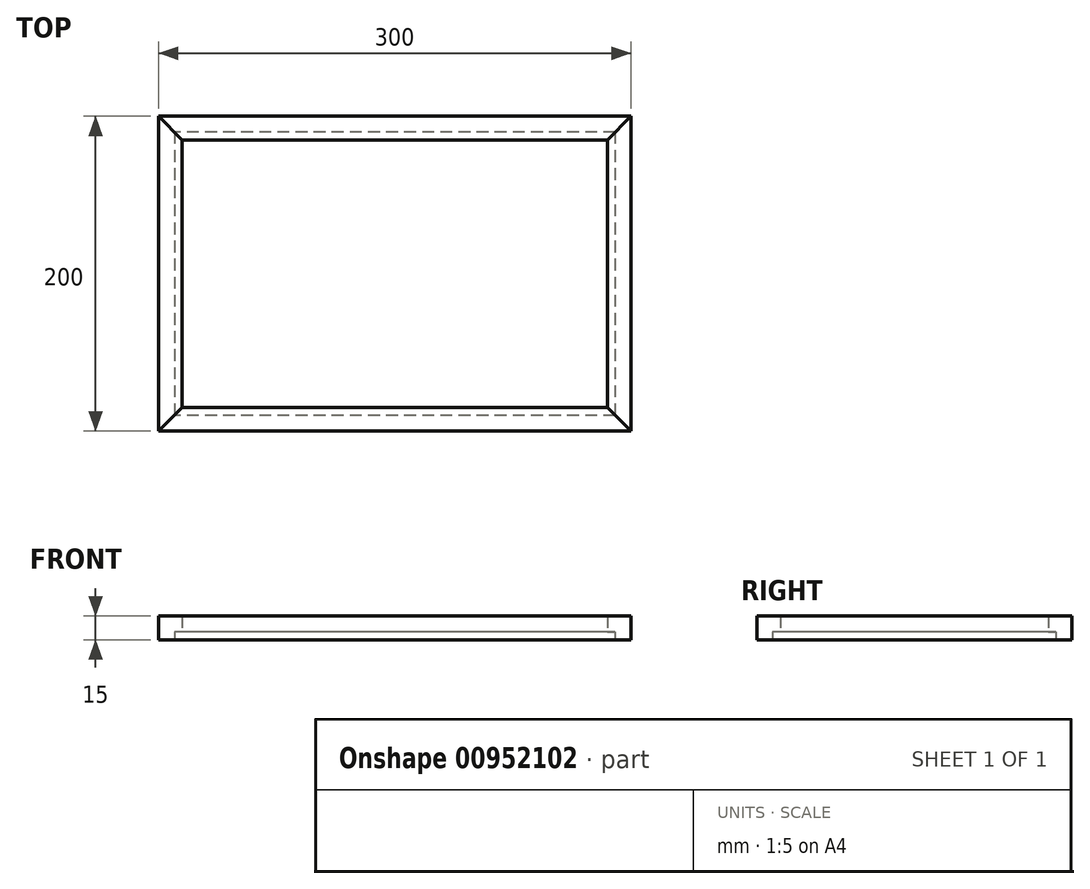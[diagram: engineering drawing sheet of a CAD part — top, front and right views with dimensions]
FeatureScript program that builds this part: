
annotation { "Feature Type Name" : "Feature", "Feature Type Description" : "" }
export const myFeature = defineFeature(function(context is Context, id is Id, definition is map)
    precondition{}
    {
        {
            var Q0;
            Q0=qCreatedBy(makeId("Top.planeOp"),FACE);
            var sketch = newSketch(context, id + "F0", { "sketchPlane" : qUnion([Q0])});
            skLineSegment(sketch, "E0.bottom", {"start": v(150, 100) * mm, "end": v(-150, 100) * mm});
            skLineSegment(sketch, "E0.top", {"start": v(150, -100) * mm, "end": v(-150, -100) * mm});
            skLineSegment(sketch, "E0.left", {"start": v(150, 100) * mm, "end": v(150, -100) * mm});
            skLineSegment(sketch, "E0.right", {"start": v(-150, 100) * mm, "end": v(-150, -100) * mm});
            skPoint(sketch, "E0.middle", {"position": v(0, 0) * mm});
            skLineSegment(sketch, "E1.0", {"start": v(135, 85) * mm, "end": v(-135, 85) * mm});
            skLineSegment(sketch, "E1.1", {"start": v(135, 85) * mm, "end": v(135, -85) * mm});
            skLineSegment(sketch, "E1.2", {"start": v(135, -85) * mm, "end": v(-135, -85) * mm});
            skLineSegment(sketch, "E1.3", {"start": v(-135, 85) * mm, "end": v(-135, -85) * mm});
            skLineSegment(sketch, "E2", {"start": v(-135, 85) * mm, "end": v(-150, 100) * mm});
            skLineSegment(sketch, "E3", {"start": v(135, 85) * mm, "end": v(150, 100) * mm});
            skLineSegment(sketch, "E4", {"start": v(135, -85) * mm, "end": v(150, -100) * mm});
            skLineSegment(sketch, "E5", {"start": v(-135, -85) * mm, "end": v(-150, -100) * mm});
            skLineSegment(sketch, "E6.0", {"start": v(140, 90) * mm, "end": v(-140, 90) * mm});
            skLineSegment(sketch, "E7.0", {"start": v(-140, 90) * mm, "end": v(-140, -90) * mm});
            skLineSegment(sketch, "E8.0", {"start": v(140, -90) * mm, "end": v(-140, -90) * mm});
            skLineSegment(sketch, "E9.0", {"start": v(140, 90) * mm, "end": v(140, -90) * mm});
            skSolve(sketch);
        }
        {
            var Q0;
            Q0=makeQuery(id+"F0.imprint","IMPRINT",FACE,{"disambiguationData":[TD([[makeQuery(id+"F0.imprint","IMPRINT",EDGE,{"derivedFrom":sQuery(id+"F0.wireOp",EDGE,"E0.bottom")}),1.0]])]});
            var Q1;
            Q1=makeQuery(id+"F0.imprint","IMPRINT",FACE,{"disambiguationData":[TD([[makeQuery(id+"F0.imprint","IMPRINT",EDGE,{"derivedFrom":sQuery(id+"F0.wireOp",EDGE,"E0.top")}),-1.0]])]});
            var Q2;
            {var subQ0=sQuery(id+"F0.wireOp",EDGE,"E1.0");Q2=makeQuery(id+"F0.imprint","IMPRINT",FACE,{"disambiguationData":[TD([[makeQuery(id+"F0.imprint","IMPRINT",EDGE,{"derivedFrom":subQ0}),-1.0]])]});}
            var Q3;
            {var subQ0=sQuery(id+"F0.wireOp",EDGE,"E1.2");Q3=makeQuery(id+"F0.imprint","IMPRINT",FACE,{"disambiguationData":[TD([[makeQuery(id+"F0.imprint","IMPRINT",EDGE,{"derivedFrom":subQ0}),1.0]])]});}
            extrude(context, id + "F1", {"entities" : qUnion([Q0, Q1, Q2, Q3]), "depth" : 15 * mm, "offsetDistance" : 25 * mm});
        }
        {
            var Q0;
            Q0=makeQuery(id+"F0.imprint","IMPRINT",FACE,{"disambiguationData":[TD([[makeQuery(id+"F0.imprint","IMPRINT",EDGE,{"derivedFrom":sQuery(id+"F0.wireOp",EDGE,"E0.right")}),1.0]])]});
            var Q1;
            Q1=makeQuery(id+"F0.imprint","IMPRINT",FACE,{"disambiguationData":[TD([[makeQuery(id+"F0.imprint","IMPRINT",EDGE,{"derivedFrom":sQuery(id+"F0.wireOp",EDGE,"E0.left")}),-1.0]])]});
            var Q2;
            {var subQ0=sQuery(id+"F0.wireOp",EDGE,"E1.3");Q2=makeQuery(id+"F0.imprint","IMPRINT",FACE,{"disambiguationData":[TD([[makeQuery(id+"F0.imprint","IMPRINT",EDGE,{"derivedFrom":subQ0}),-1.0]])]});}
            var Q3;
            {var subQ0=sQuery(id+"F0.wireOp",EDGE,"E1.1");Q3=makeQuery(id+"F0.imprint","IMPRINT",FACE,{"disambiguationData":[TD([[makeQuery(id+"F0.imprint","IMPRINT",EDGE,{"derivedFrom":subQ0}),1.0]])]});}
            extrude(context, id + "F2", {"entities" : qUnion([Q0, Q1, Q2, Q3]), "depth" : 15 * mm, "offsetDistance" : 25 * mm});
        }
        {
            var Q0;
            {var subQ0=sQuery(id+"F0.wireOp",EDGE,"E1.2");Q0=makeQuery(id+"F0.imprint","IMPRINT",FACE,{"disambiguationData":[TD([[makeQuery(id+"F0.imprint","IMPRINT",EDGE,{"derivedFrom":subQ0}),1.0]])]});}
            var Q1;
            {var subQ0=sQuery(id+"F0.wireOp",EDGE,"E1.1");Q1=makeQuery(id+"F0.imprint","IMPRINT",FACE,{"disambiguationData":[TD([[makeQuery(id+"F0.imprint","IMPRINT",EDGE,{"derivedFrom":subQ0}),1.0]])]});}
            var Q2;
            {var subQ0=sQuery(id+"F0.wireOp",EDGE,"E1.0");Q2=makeQuery(id+"F0.imprint","IMPRINT",FACE,{"disambiguationData":[TD([[makeQuery(id+"F0.imprint","IMPRINT",EDGE,{"derivedFrom":subQ0}),-1.0]])]});}
            var Q3;
            {var subQ0=sQuery(id+"F0.wireOp",EDGE,"E1.3");Q3=makeQuery(id+"F0.imprint","IMPRINT",FACE,{"disambiguationData":[TD([[makeQuery(id+"F0.imprint","IMPRINT",EDGE,{"derivedFrom":subQ0}),-1.0]])]});}
            extrude(context, id + "F3", {"entities" : qUnion([Q0, Q1, Q2, Q3]), "operationType" : NewBodyOperationType.REMOVE, "depth" : 5 * mm, "offsetDistance" : 25 * mm});
        }
        {
            var Q0;
            Q0=makeQuery(id+"F0.imprint","IMPRINT",FACE,{"disambiguationData":[TD([[makeQuery(id+"F0.imprint","IMPRINT",EDGE,{"derivedFrom":sQuery(id+"F0.wireOp",EDGE,"E1.0")}),1.0]])]});
            var Q1;
            {var subQ0=sQuery(id+"F0.wireOp",EDGE,"E1.0");Q1=makeQuery(id+"F0.imprint","IMPRINT",FACE,{"disambiguationData":[TD([[makeQuery(id+"F0.imprint","IMPRINT",EDGE,{"derivedFrom":subQ0}),-1.0]])]});}
            var Q2;
            {var subQ0=sQuery(id+"F0.wireOp",EDGE,"E1.1");Q2=makeQuery(id+"F0.imprint","IMPRINT",FACE,{"disambiguationData":[TD([[makeQuery(id+"F0.imprint","IMPRINT",EDGE,{"derivedFrom":subQ0}),1.0]])]});}
            var Q3;
            {var subQ0=sQuery(id+"F0.wireOp",EDGE,"E1.2");Q3=makeQuery(id+"F0.imprint","IMPRINT",FACE,{"disambiguationData":[TD([[makeQuery(id+"F0.imprint","IMPRINT",EDGE,{"derivedFrom":subQ0}),1.0]])]});}
            var Q4;
            {var subQ0=sQuery(id+"F0.wireOp",EDGE,"E1.3");Q4=makeQuery(id+"F0.imprint","IMPRINT",FACE,{"disambiguationData":[TD([[makeQuery(id+"F0.imprint","IMPRINT",EDGE,{"derivedFrom":subQ0}),-1.0]])]});}
            extrude(context, id + "F4", {"entities" : qUnion([Q0, Q1, Q2, Q3, Q4]), "depth" : 5 * mm, "offsetDistance" : 25 * mm});
        }
    });
